# Revit family: HVAC_Ortal_Fireplace_Wilderness_Stand-Alone-Three-Sided
name_source: partatom
category: Specialty Equipment
units: mm (PartAtom-declared; Revit-internal decimal feet)

## family parameters
Always vertical = Yes
Cut with Voids When Loaded = No
OmniClass Number = 23.40.20.34.14
OmniClass Title = Fireplaces
Part Type = Normal
Room Calculation Point = No
Round Connector Dimension = Use Diameter
Shared = No
Work Plane-Based = No

## types (2) — shared parameters
Apparent Load = 750 VA
Assembly Code = E1090400
Certification = ANSI Z21.88/CSA 2.33-2019
Current = 15 A
Depth = 22 5/16"
Edition number = 1
Efficiency = 79.7%
Frequency = 60 Hz
Gas Flow = 0 GPM
Gas Inlet Diameter = 1/2"
Gas Type = Gas : Natural Gas
Height = 36 39/64"
Interior Material = Ortal - Panel - Black Reflective Glass
Keynote = 15500
Manufacturer = Ortal
Number of Poles = 3
Power Factor = 0.8
Product Guid = d18e7cdc-3d85-48d4-a96d-959020e9328d
Product Material = Ortal - Stainless Steel - Black
Product data url = https://www.bimobject.com
Total Heating Capacity = 32768.0 Btu/h
URL = https://www.ortalheat.com
Vent = 5x8 co-axial direct vent pipe (5” interior, 8” exterior)
Viewing Area Height = 23 3/4"
Viewing Area Side Length = 18 3/4"
Viewing Area Width = 28 9/16"
Voltage = 120 V
Weight = 331.00 lbf
Width = 28 9/16"
z_Frame Thickness = 5/32"
z_Gas Type 1 = Gas : Natural Gas
z_Gas Type 2 = Gas : Propane
z_Glass Offset = 2"
z_Glass Thickness = 5/32"
z_Side Glass Offset Front = 2 5/32"

## per-type parameters (varying)
| type | Description |
| Wilderness Stand Alone Three Sided 25H - Wall Mount | Wilderness Type Stand Alone Three Sided Fireplace Wall Mounted |
| Wilderness Stand Alone Three Sided 25H - Floor Mount | Wilderness Type Stand Alone Three Sided Fireplace Floor Mounted |

note: column(s) folded — value = type name in every type: Model

## geometry (parser evidence)
native form markers: Sweep x4
no freeform markers — native parametric forms only
